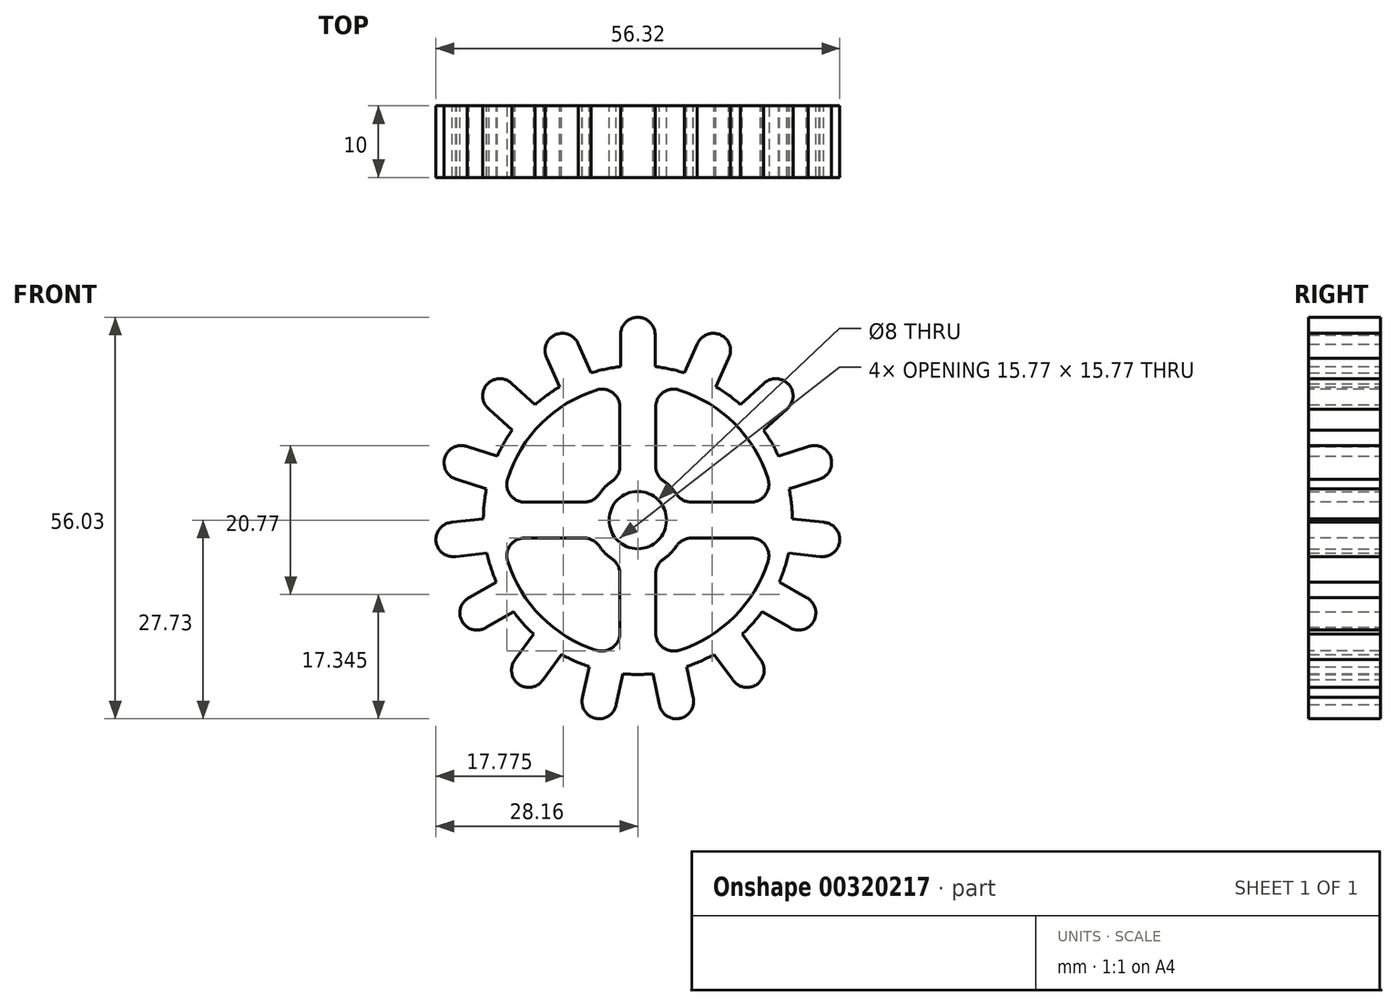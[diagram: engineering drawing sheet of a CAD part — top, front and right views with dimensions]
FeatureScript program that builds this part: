
annotation { "Feature Type Name" : "Feature", "Feature Type Description" : "" }
export const myFeature = defineFeature(function(context is Context, id is Id, definition is map)
    precondition{}
    {
        {
            var Q0;
            Q0=qCreatedBy(makeId("Front.planeOp"),FACE);
            var sketch = newSketch(context, id + "F0", { "sketchPlane" : qUnion([Q0])});
            skCircle(sketch, "E0", {"center": v(0, 0) * mm, "radius": 4 * mm});
            skArc(sketch, "E1", {"start": v(-10.9, 18.59) * mm, "mid": v(-12.67, 17.43) * mm, "end": v(-14.31, 16.11) * mm});
            skArc(sketch, "E2", {"start": v(2.4, 25.79) * mm, "mid": v(0, 28.3) * mm, "end": v(-2.4, 25.79) * mm});
            skLineSegment(sketch, "E3", {"start": v(2.4, 25.79) * mm, "end": v(2.4, 21.42) * mm});
            skLineSegment(sketch, "E4", {"start": v(-2.4, 25.79) * mm, "end": v(-2.4, 21.42) * mm});
            skLineSegment(sketch, "E5.1.0", {"start": v(-8.3, 24.53) * mm, "end": v(-6.52, 20.54) * mm});
            skArc(sketch, "E5.1.1", {"start": v(-8.3, 24.53) * mm, "mid": v(-11.51, 25.85) * mm, "end": v(-12.68, 22.58) * mm});
            skLineSegment(sketch, "E5.1.2", {"start": v(-12.68, 22.58) * mm, "end": v(-10.9, 18.59) * mm});
            skLineSegment(sketch, "E5.2.0", {"start": v(-17.56, 19.04) * mm, "end": v(-14.31, 16.11) * mm});
            skArc(sketch, "E5.2.1", {"start": v(-17.56, 19.04) * mm, "mid": v(-21.03, 18.94) * mm, "end": v(-20.77, 15.47) * mm});
            skLineSegment(sketch, "E5.2.2", {"start": v(-20.77, 15.47) * mm, "end": v(-17.52, 12.55) * mm});
            skLineSegment(sketch, "E5.3.0", {"start": v(-23.79, 10.25) * mm, "end": v(-19.63, 8.9) * mm});
            skArc(sketch, "E5.3.1", {"start": v(-23.79, 10.25) * mm, "mid": v(-26.91, 8.75) * mm, "end": v(-25.27, 5.69) * mm});
            skLineSegment(sketch, "E5.3.2", {"start": v(-25.27, 5.69) * mm, "end": v(-21.1, 4.34) * mm});
            skLineSegment(sketch, "E5.4.0", {"start": v(-25.9, -0.31) * mm, "end": v(-21.55, 0.15) * mm});
            skArc(sketch, "E5.4.1", {"start": v(-25.9, -0.31) * mm, "mid": v(-28.14, -2.96) * mm, "end": v(-25.4, -5.08) * mm});
            skLineSegment(sketch, "E5.4.2", {"start": v(-25.4, -5.08) * mm, "end": v(-21.05, -4.62) * mm});
            skLineSegment(sketch, "E5.5.0", {"start": v(-23.53, -10.82) * mm, "end": v(-19.75, -8.63) * mm});
            skArc(sketch, "E5.5.1", {"start": v(-23.53, -10.82) * mm, "mid": v(-24.5, -14.15) * mm, "end": v(-21.14, -14.97) * mm});
            skLineSegment(sketch, "E5.5.2", {"start": v(-21.14, -14.97) * mm, "end": v(-17.35, -12.78) * mm});
            skLineSegment(sketch, "E5.6.0", {"start": v(-17.1, -19.45) * mm, "end": v(-14.53, -15.92) * mm});
            skArc(sketch, "E5.6.1", {"start": v(-17.1, -19.45) * mm, "mid": v(-16.63, -22.9) * mm, "end": v(-13.22, -22.27) * mm});
            skLineSegment(sketch, "E5.6.2", {"start": v(-13.22, -22.27) * mm, "end": v(-10.65, -18.74) * mm});
            skLineSegment(sketch, "E5.7.0", {"start": v(-7.7, -24.73) * mm, "end": v(-6.8, -20.45) * mm});
            skArc(sketch, "E5.7.1", {"start": v(-7.7, -24.73) * mm, "mid": v(-5.88, -27.68) * mm, "end": v(-3.02, -25.72) * mm});
            skLineSegment(sketch, "E5.7.2", {"start": v(-3.02, -25.72) * mm, "end": v(-2.1, -21.45) * mm});
            skLineSegment(sketch, "E5.8.0", {"start": v(3.02, -25.72) * mm, "end": v(2.1, -21.45) * mm});
            skArc(sketch, "E5.8.1", {"start": v(3.02, -25.72) * mm, "mid": v(5.88, -27.68) * mm, "end": v(7.7, -24.73) * mm});
            skLineSegment(sketch, "E5.8.2", {"start": v(7.7, -24.73) * mm, "end": v(6.8, -20.45) * mm});
            skLineSegment(sketch, "E5.9.0", {"start": v(13.22, -22.27) * mm, "end": v(10.65, -18.74) * mm});
            skArc(sketch, "E5.9.1", {"start": v(13.22, -22.27) * mm, "mid": v(16.63, -22.9) * mm, "end": v(17.1, -19.45) * mm});
            skLineSegment(sketch, "E5.9.2", {"start": v(17.1, -19.45) * mm, "end": v(14.53, -15.92) * mm});
            skLineSegment(sketch, "E5.10.0", {"start": v(21.14, -14.97) * mm, "end": v(17.35, -12.78) * mm});
            skArc(sketch, "E5.10.1", {"start": v(21.14, -14.97) * mm, "mid": v(24.5, -14.15) * mm, "end": v(23.53, -10.82) * mm});
            skLineSegment(sketch, "E5.10.2", {"start": v(23.53, -10.82) * mm, "end": v(19.75, -8.63) * mm});
            skLineSegment(sketch, "E5.11.0", {"start": v(25.4, -5.08) * mm, "end": v(21.05, -4.62) * mm});
            skArc(sketch, "E5.11.1", {"start": v(25.4, -5.08) * mm, "mid": v(28.14, -2.96) * mm, "end": v(25.9, -0.31) * mm});
            skLineSegment(sketch, "E5.11.2", {"start": v(25.9, -0.31) * mm, "end": v(21.55, 0.15) * mm});
            skLineSegment(sketch, "E5.12.0", {"start": v(25.27, 5.69) * mm, "end": v(21.1, 4.34) * mm});
            skArc(sketch, "E5.12.1", {"start": v(25.27, 5.69) * mm, "mid": v(26.91, 8.75) * mm, "end": v(23.79, 10.25) * mm});
            skLineSegment(sketch, "E5.12.2", {"start": v(23.79, 10.25) * mm, "end": v(19.63, 8.9) * mm});
            skLineSegment(sketch, "E5.13.0", {"start": v(20.77, 15.47) * mm, "end": v(17.52, 12.55) * mm});
            skArc(sketch, "E5.13.1", {"start": v(20.77, 15.47) * mm, "mid": v(21.03, 18.94) * mm, "end": v(17.56, 19.04) * mm});
            skLineSegment(sketch, "E5.13.2", {"start": v(17.56, 19.04) * mm, "end": v(14.31, 16.11) * mm});
            skLineSegment(sketch, "E5.14.0", {"start": v(12.68, 22.58) * mm, "end": v(10.9, 18.59) * mm});
            skArc(sketch, "E5.14.1", {"start": v(12.68, 22.58) * mm, "mid": v(11.51, 25.85) * mm, "end": v(8.3, 24.53) * mm});
            skLineSegment(sketch, "E5.14.2", {"start": v(8.3, 24.53) * mm, "end": v(6.52, 20.54) * mm});
            skArc(sketch, "E6.trimOffspring", {"start": v(-17.52, 12.55) * mm, "mid": v(-18.66, 10.78) * mm, "end": v(-19.63, 8.9) * mm});
            skArc(sketch, "E7.trimOffspring", {"start": v(-21.1, 4.34) * mm, "mid": v(-21.43, 2.25) * mm, "end": v(-21.55, 0.15) * mm});
            skArc(sketch, "E8.trimOffspring", {"start": v(-21.05, -4.62) * mm, "mid": v(-20.5, -6.66) * mm, "end": v(-19.75, -8.63) * mm});
            skArc(sketch, "E9.trimOffspring", {"start": v(-17.35, -12.78) * mm, "mid": v(-16.01, -14.42) * mm, "end": v(-14.53, -15.92) * mm});
            skArc(sketch, "E10.trimOffspring", {"start": v(-10.65, -18.74) * mm, "mid": v(-8.77, -19.69) * mm, "end": v(-6.8, -20.45) * mm});
            skArc(sketch, "E11.trimOffspring", {"start": v(-2.1, -21.45) * mm, "mid": v(0, -21.55) * mm, "end": v(2.1, -21.45) * mm});
            skArc(sketch, "E12.trimOffspring", {"start": v(6.8, -20.45) * mm, "mid": v(8.77, -19.69) * mm, "end": v(10.65, -18.74) * mm});
            skArc(sketch, "E13.trimOffspring", {"start": v(14.53, -15.92) * mm, "mid": v(16.01, -14.42) * mm, "end": v(17.35, -12.78) * mm});
            skArc(sketch, "E14.trimOffspring", {"start": v(19.75, -8.63) * mm, "mid": v(20.5, -6.66) * mm, "end": v(21.05, -4.62) * mm});
            skArc(sketch, "E15.trimOffspring", {"start": v(21.55, 0.15) * mm, "mid": v(21.43, 2.25) * mm, "end": v(21.1, 4.34) * mm});
            skArc(sketch, "E16.trimOffspring", {"start": v(19.63, 8.9) * mm, "mid": v(18.66, 10.78) * mm, "end": v(17.52, 12.55) * mm});
            skArc(sketch, "E17.trimOffspring", {"start": v(14.31, 16.11) * mm, "mid": v(12.67, 17.43) * mm, "end": v(10.9, 18.59) * mm});
            skArc(sketch, "E18.trimOffspring", {"start": v(6.52, 20.54) * mm, "mid": v(4.48, 21.08) * mm, "end": v(2.4, 21.42) * mm});
            skArc(sketch, "E19.trimOffspring", {"start": v(-2.4, 21.42) * mm, "mid": v(-4.48, 21.08) * mm, "end": v(-6.52, 20.54) * mm});
            skSolve(sketch);
        }
        {
            var Q0;
            Q0 = qSketchRegion(id + "F0", true);
            extrude(context, id + "F1", {"entities" : qUnion([Q0]), "endBound" : BoundingType.SYMMETRIC, "depth" : 10 * mm});
        }
        {
            var Q0;
            Q0=makeQuery(id+"F1.opExtrude","CAP_FACE",FACE,{"disambiguationData":[OSD([sQuery(id+"F0.wireOp",EDGE,"E0"),sQuery(id+"F0.wireOp",EDGE,"E1"),sQuery(id+"F0.wireOp",EDGE,"E2"),sQuery(id+"F0.wireOp",EDGE,"E3"),sQuery(id+"F0.wireOp",EDGE,"E4"),sQuery(id+"F0.wireOp",EDGE,"E5.1.0"),sQuery(id+"F0.wireOp",EDGE,"E5.1.1"),sQuery(id+"F0.wireOp",EDGE,"E5.1.2"),sQuery(id+"F0.wireOp",EDGE,"E5.2.0"),sQuery(id+"F0.wireOp",EDGE,"E5.2.1"),sQuery(id+"F0.wireOp",EDGE,"E5.2.2"),sQuery(id+"F0.wireOp",EDGE,"E5.3.0"),sQuery(id+"F0.wireOp",EDGE,"E5.3.1"),sQuery(id+"F0.wireOp",EDGE,"E5.3.2"),sQuery(id+"F0.wireOp",EDGE,"E5.4.0"),sQuery(id+"F0.wireOp",EDGE,"E5.4.1"),sQuery(id+"F0.wireOp",EDGE,"E5.4.2"),sQuery(id+"F0.wireOp",EDGE,"E5.5.0"),sQuery(id+"F0.wireOp",EDGE,"E5.5.1"),sQuery(id+"F0.wireOp",EDGE,"E5.5.2"),sQuery(id+"F0.wireOp",EDGE,"E5.6.0"),sQuery(id+"F0.wireOp",EDGE,"E5.6.1"),sQuery(id+"F0.wireOp",EDGE,"E5.6.2"),sQuery(id+"F0.wireOp",EDGE,"E5.7.0"),sQuery(id+"F0.wireOp",EDGE,"E5.7.1"),sQuery(id+"F0.wireOp",EDGE,"E5.7.2"),sQuery(id+"F0.wireOp",EDGE,"E5.8.0"),sQuery(id+"F0.wireOp",EDGE,"E5.8.1"),sQuery(id+"F0.wireOp",EDGE,"E5.8.2"),sQuery(id+"F0.wireOp",EDGE,"E5.9.0"),sQuery(id+"F0.wireOp",EDGE,"E5.9.1"),sQuery(id+"F0.wireOp",EDGE,"E5.9.2"),sQuery(id+"F0.wireOp",EDGE,"E5.10.0"),sQuery(id+"F0.wireOp",EDGE,"E5.10.1"),sQuery(id+"F0.wireOp",EDGE,"E5.10.2"),sQuery(id+"F0.wireOp",EDGE,"E5.11.0"),sQuery(id+"F0.wireOp",EDGE,"E5.11.1"),sQuery(id+"F0.wireOp",EDGE,"E5.11.2"),sQuery(id+"F0.wireOp",EDGE,"E5.12.0"),sQuery(id+"F0.wireOp",EDGE,"E5.12.1"),sQuery(id+"F0.wireOp",EDGE,"E5.12.2"),sQuery(id+"F0.wireOp",EDGE,"E5.13.0"),sQuery(id+"F0.wireOp",EDGE,"E5.13.1"),sQuery(id+"F0.wireOp",EDGE,"E5.13.2"),sQuery(id+"F0.wireOp",EDGE,"E5.14.0"),sQuery(id+"F0.wireOp",EDGE,"E5.14.1"),sQuery(id+"F0.wireOp",EDGE,"E5.14.2"),sQuery(id+"F0.wireOp",EDGE,"E6.trimOffspring"),sQuery(id+"F0.wireOp",EDGE,"E7.trimOffspring"),sQuery(id+"F0.wireOp",EDGE,"E8.trimOffspring"),sQuery(id+"F0.wireOp",EDGE,"E9.trimOffspring"),sQuery(id+"F0.wireOp",EDGE,"E10.trimOffspring"),sQuery(id+"F0.wireOp",EDGE,"E11.trimOffspring"),sQuery(id+"F0.wireOp",EDGE,"E12.trimOffspring"),sQuery(id+"F0.wireOp",EDGE,"E13.trimOffspring"),sQuery(id+"F0.wireOp",EDGE,"E14.trimOffspring"),sQuery(id+"F0.wireOp",EDGE,"E15.trimOffspring"),sQuery(id+"F0.wireOp",EDGE,"E16.trimOffspring"),sQuery(id+"F0.wireOp",EDGE,"E17.trimOffspring"),sQuery(id+"F0.wireOp",EDGE,"E18.trimOffspring"),sQuery(id+"F0.wireOp",EDGE,"E19.trimOffspring")])],"isStart":false});
            var sketch = newSketch(context, id + "F2", { "sketchPlane" : qUnion([Q0])});
            skArc(sketch, "E20", {"start": v(-18.16, 5.76) * mm, "mid": v(-13.47, 13.47) * mm, "end": v(-5.76, 18.16) * mm});
            skLineSegment(sketch, "E21", {"start": v(0, 0) * mm, "end": v(0, 23.63) * mm, "construction": true});
            skLineSegment(sketch, "E22", {"start": v(0, 23.63) * mm, "end": v(0, 19.05) * mm, "construction": true});
            skLineSegment(sketch, "E23", {"start": v(0, 0) * mm, "end": v(-36.4, 0) * mm, "construction": true});
            skLineSegment(sketch, "E24", {"start": v(-2.5, 15.78) * mm, "end": v(-2.5, 7.48) * mm});
            skLineSegment(sketch, "E25", {"start": v(-15.78, 2.5) * mm, "end": v(-7.48, 2.5) * mm});
            skArc(sketch, "E26.trimOffspring", {"start": v(-3.61, 5.4) * mm, "mid": v(-4.6, 4.6) * mm, "end": v(-5.4, 3.61) * mm});
            skPoint(sketch, "E27.orphan", {"position": v(0, 19.05) * mm});
            skPoint(sketch, "E28.orphan", {"position": v(-19.05, 0) * mm});
            skPoint(sketch, "E29.visualSharp", {"position": v(-2.5, 18.89) * mm});
            skArc(sketch, "E29.filletArc", {"start": v(-2.5, 15.78) * mm, "mid": v(-3.52, 17.8) * mm, "end": v(-5.76, 18.16) * mm});
            skPoint(sketch, "E30.visualSharp", {"position": v(-18.89, 2.5) * mm});
            skArc(sketch, "E30.filletArc", {"start": v(-18.16, 5.76) * mm, "mid": v(-17.8, 3.52) * mm, "end": v(-15.78, 2.5) * mm});
            skPoint(sketch, "E31.visualSharp", {"position": v(-6, 2.5) * mm});
            skArc(sketch, "E31.filletArc", {"start": v(-7.48, 2.5) * mm, "mid": v(-6.3, 2.8) * mm, "end": v(-5.4, 3.61) * mm});
            skPoint(sketch, "E32.visualSharp", {"position": v(-2.5, 6) * mm});
            skArc(sketch, "E32.filletArc", {"start": v(-3.61, 5.4) * mm, "mid": v(-2.8, 6.3) * mm, "end": v(-2.5, 7.48) * mm});
            skArc(sketch, "E33.MirrorCS", {"start": v(2.5, 15.78) * mm, "mid": v(3.52, 17.8) * mm, "end": v(5.76, 18.16) * mm});
            skArc(sketch, "E34.MirrorCS", {"start": v(18.16, 5.76) * mm, "mid": v(13.47, 13.47) * mm, "end": v(5.76, 18.16) * mm});
            skArc(sketch, "E35.MirrorCS", {"start": v(18.16, 5.76) * mm, "mid": v(17.8, 3.52) * mm, "end": v(15.78, 2.5) * mm});
            skLineSegment(sketch, "E36.MirrorCS", {"start": v(15.78, 2.5) * mm, "end": v(7.48, 2.5) * mm});
            skArc(sketch, "E37.MirrorCS", {"start": v(7.48, 2.5) * mm, "mid": v(6.3, 2.8) * mm, "end": v(5.4, 3.61) * mm});
            skArc(sketch, "E38.MirrorCS", {"start": v(3.61, 5.4) * mm, "mid": v(4.6, 4.6) * mm, "end": v(5.4, 3.61) * mm});
            skArc(sketch, "E39.MirrorCS", {"start": v(3.61, 5.4) * mm, "mid": v(2.8, 6.3) * mm, "end": v(2.5, 7.48) * mm});
            skLineSegment(sketch, "E40.MirrorCS", {"start": v(2.5, 15.78) * mm, "end": v(2.5, 7.48) * mm});
            skLineSegment(sketch, "E41.0", {"start": v(0, 5) * mm, "end": v(-18.28, 5) * mm});
            skLineSegment(sketch, "E42.MirrorCS", {"start": v(-15.78, -2.5) * mm, "end": v(-7.48, -2.5) * mm});
            skArc(sketch, "E43.MirrorCS", {"start": v(-18.16, -5.76) * mm, "mid": v(-17.8, -3.52) * mm, "end": v(-15.78, -2.5) * mm});
            skArc(sketch, "E44.MirrorCS", {"start": v(-18.16, -5.76) * mm, "mid": v(-13.47, -13.47) * mm, "end": v(-5.76, -18.16) * mm});
            skArc(sketch, "E45.MirrorCS", {"start": v(-2.5, -15.78) * mm, "mid": v(-3.52, -17.8) * mm, "end": v(-5.76, -18.16) * mm});
            skLineSegment(sketch, "E46.MirrorCS", {"start": v(-2.5, -15.78) * mm, "end": v(-2.5, -7.48) * mm});
            skPoint(sketch, "E47.MirrorP", {"position": v(-2.5, -6) * mm});
            skArc(sketch, "E48.MirrorCS", {"start": v(-3.61, -5.4) * mm, "mid": v(-4.6, -4.6) * mm, "end": v(-5.4, -3.61) * mm});
            skArc(sketch, "E49.MirrorCS", {"start": v(-3.61, -5.4) * mm, "mid": v(-2.8, -6.3) * mm, "end": v(-2.5, -7.48) * mm});
            skArc(sketch, "E50.MirrorCS", {"start": v(-7.48, -2.5) * mm, "mid": v(-6.3, -2.8) * mm, "end": v(-5.4, -3.61) * mm});
            skArc(sketch, "E51.MirrorCS", {"start": v(3.61, -5.4) * mm, "mid": v(2.8, -6.3) * mm, "end": v(2.5, -7.48) * mm});
            skLineSegment(sketch, "E52.MirrorCS", {"start": v(2.5, -15.78) * mm, "end": v(2.5, -7.48) * mm});
            skArc(sketch, "E53.MirrorCS", {"start": v(2.5, -15.78) * mm, "mid": v(3.52, -17.8) * mm, "end": v(5.76, -18.16) * mm});
            skArc(sketch, "E54.MirrorCS", {"start": v(18.16, -5.76) * mm, "mid": v(13.47, -13.47) * mm, "end": v(5.76, -18.16) * mm});
            skArc(sketch, "E55.MirrorCS", {"start": v(18.16, -5.76) * mm, "mid": v(17.8, -3.52) * mm, "end": v(15.78, -2.5) * mm});
            skLineSegment(sketch, "E56.MirrorCS", {"start": v(15.78, -2.5) * mm, "end": v(7.48, -2.5) * mm});
            skArc(sketch, "E57.MirrorCS", {"start": v(7.48, -2.5) * mm, "mid": v(6.3, -2.8) * mm, "end": v(5.4, -3.61) * mm});
            skArc(sketch, "E58.MirrorCS", {"start": v(3.61, -5.4) * mm, "mid": v(4.6, -4.6) * mm, "end": v(5.4, -3.61) * mm});
            skLineSegment(sketch, "E59.trimOffspring", {"start": v(0, 5) * mm, "end": v(0, 0) * mm, "construction": true});
            skSolve(sketch);
        }
        {
            var Q0;
            Q0 = qSketchRegion(id + "F2", true);
            extrude(context, id + "F3", {"entities" : qUnion([Q0]), "operationType" : NewBodyOperationType.REMOVE, "oppositeDirection" : true, "depth" : 10 * mm});
        }
    });
